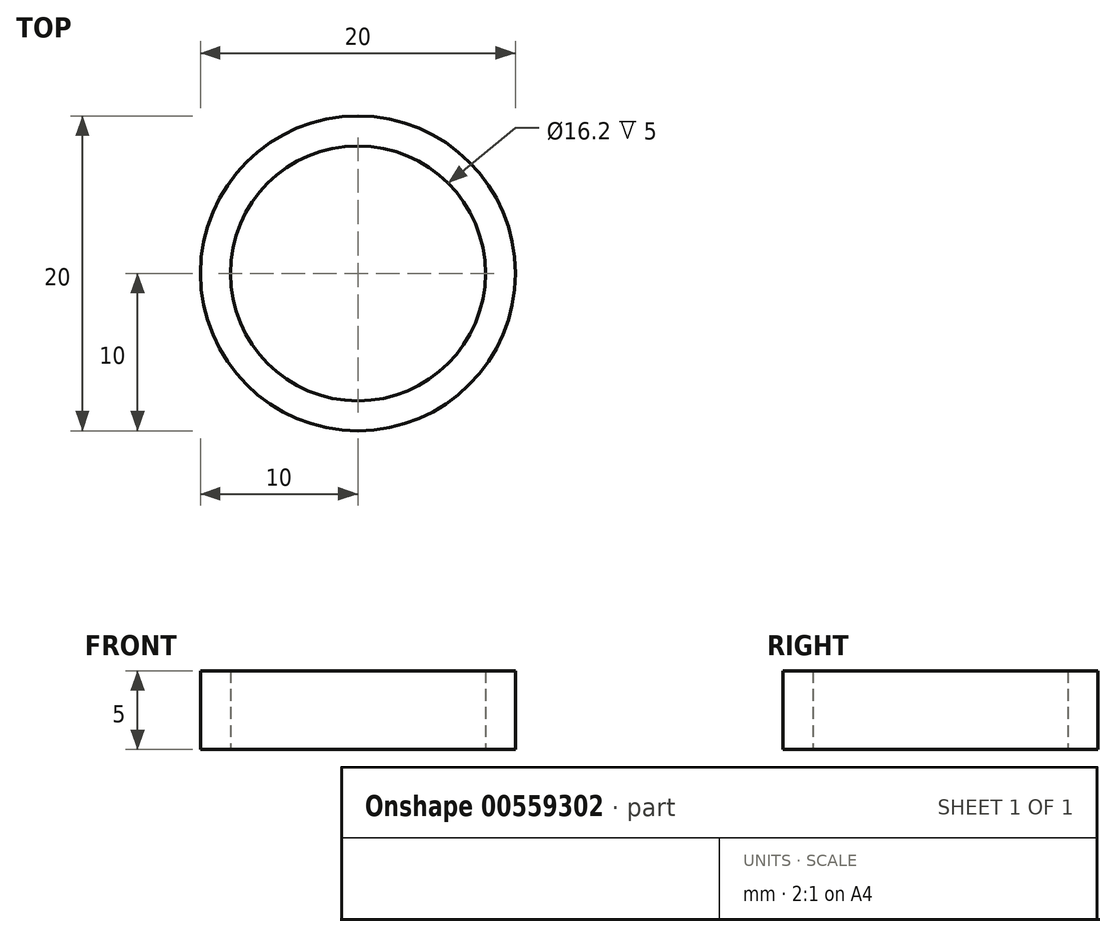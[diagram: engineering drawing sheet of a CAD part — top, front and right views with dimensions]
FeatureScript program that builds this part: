
annotation { "Feature Type Name" : "Feature", "Feature Type Description" : "" }
export const myFeature = defineFeature(function(context is Context, id is Id, definition is map)
    precondition{}
    {
        {
            var Q0;
            Q0=qCreatedBy(makeId("Top.planeOp"),FACE);
            var sketch = newSketch(context, id + "F0", { "sketchPlane" : qUnion([Q0])});
            skCircle(sketch, "E0", {"center": v(0, 0) * mm, "radius": 8.1 * mm});
            skCircle(sketch, "E1", {"center": v(0, 0) * mm, "radius": 10 * mm});
            skSolve(sketch);
        }
        {
            var Q0;
            Q0 = qSketchRegion(id + "F0", true);
            extrude(context, id + "F1", {"entities" : qUnion([Q0]), "depth" : 5 * mm, "offsetDistance" : 25 * mm});
        }
    });
